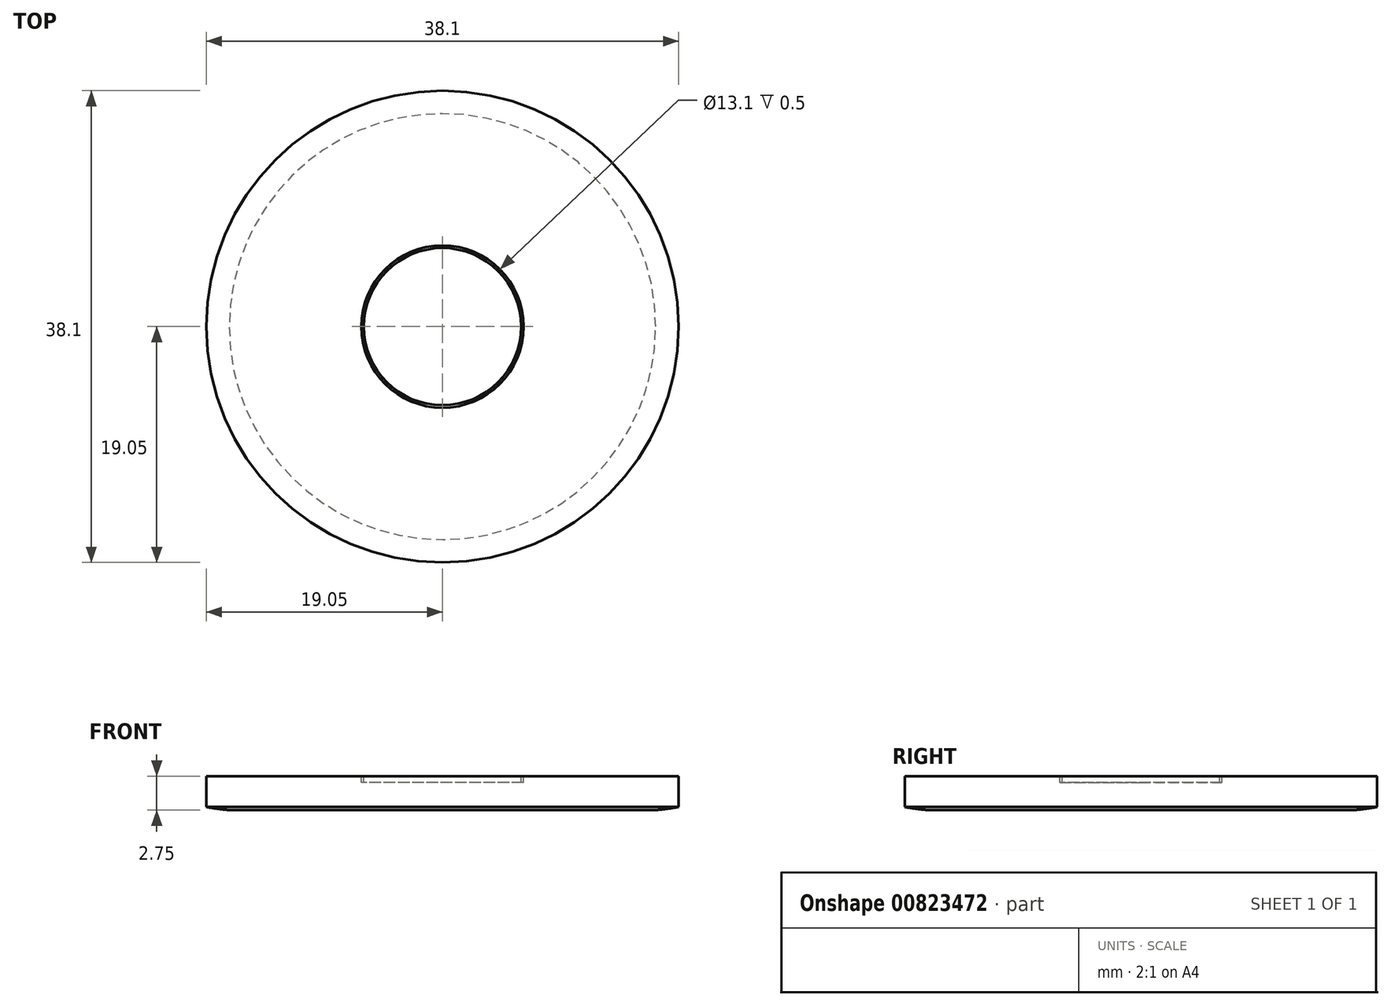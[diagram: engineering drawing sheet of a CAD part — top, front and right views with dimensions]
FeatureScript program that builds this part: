
annotation { "Feature Type Name" : "Feature", "Feature Type Description" : "" }
export const myFeature = defineFeature(function(context is Context, id is Id, definition is map)
    precondition{}
    {
        {
            var Q0;
            Q0=qCreatedBy(makeId("Top.planeOp"),FACE);
            var sketch = newSketch(context, id + "F0", { "sketchPlane" : qUnion([Q0])});
            skCircle(sketch, "E0", {"center": v(0, 0) * mm, "radius": 19.05 * mm});
            skSolve(sketch);
        }
        {
            var Q0;
            Q0=makeQuery(id+"F0.imprint","IMPRINT",FACE,{"disambiguationData":[TD([[makeQuery(id+"F0.imprint","IMPRINT",EDGE,{"derivedFrom":sQuery(id+"F0.wireOp",EDGE,"E0")}),1.0]])]});
            extrude(context, id + "F1", {"entities" : qUnion([Q0]), "depth" : 2.5 * mm, "offsetDistance" : 25 * mm});
        }
        {
            var Q0;
            Q0=makeQuery(id+"F1.opExtrude","CAP_FACE",FACE,{"disambiguationData":[OSD([sQuery(id+"F0.wireOp",EDGE,"E0")])],"isStart":false});
            var sketch = newSketch(context, id + "F2", { "sketchPlane" : qUnion([Q0])});
            skCircle(sketch, "E1", {"center": v(0, 0) * mm, "radius": 6.35 * mm});
            skCircle(sketch, "E2", {"center": v(0, 0) * mm, "radius": 6.55 * mm});
            skSolve(sketch);
        }
        {
            var Q0;
            Q0=makeQuery(id+"F2.imprint","IMPRINT",FACE,{"disambiguationData":[TD([[makeQuery(id+"F2.imprint","IMPRINT",EDGE,{"derivedFrom":sQuery(id+"F2.wireOp",EDGE,"E1")}),-1.0]])]});
            extrude(context, id + "F3", {"entities" : qUnion([Q0]), "operationType" : NewBodyOperationType.REMOVE, "oppositeDirection" : true, "depth" : .5 * mm, "offsetDistance" : 25 * mm});
        }
        {
            var Q0;
            Q0=qCreatedBy(makeId("Front.planeOp"),FACE);
            var sketch = newSketch(context, id + "F4", { "sketchPlane" : qUnion([Q0])});
            skLineSegment(sketch, "E3.0", {"start": v(-19.05, 0) * mm, "end": v(0, 0) * mm});
            skLineSegment(sketch, "E4", {"start": v(0, 0) * mm, "end": v(0, -0.25) * mm});
            skArc(sketch, "E5", {"start": v(-19.05, 0) * mm, "mid": v(-18.12, -0.14) * mm, "end": v(-17.2, -0.25) * mm});
            skLineSegment(sketch, "E6", {"start": v(0, -0.25) * mm, "end": v(-17.2, -0.25) * mm});
            skPoint(sketch, "E7.orphan", {"position": v(0, -0.5) * mm});
            skPoint(sketch, "E8.orphan", {"position": v(19.05, 0) * mm});
            skSolve(sketch);
        }
        {
            var Q0;
            Q0=makeQuery(id+"F4.imprint","IMPRINT",FACE,{"disambiguationData":[TD([[makeQuery(id+"F4.imprint","IMPRINT",EDGE,{"derivedFrom":sQuery(id+"F4.wireOp",EDGE,"E3.0")}),-1.0]])]});
            var Q1;
            Q1=sQuery(id+"F4.wireOp",EDGE,"E4");
            revolve(context, id + "F5", {"surfaceOperationType" : NewSurfaceOperationType.NEW, "entities" : qUnion([Q0]), "axis" : qUnion([Q1]), "revolveType" : RevolveType.FULL});
        }
    });
